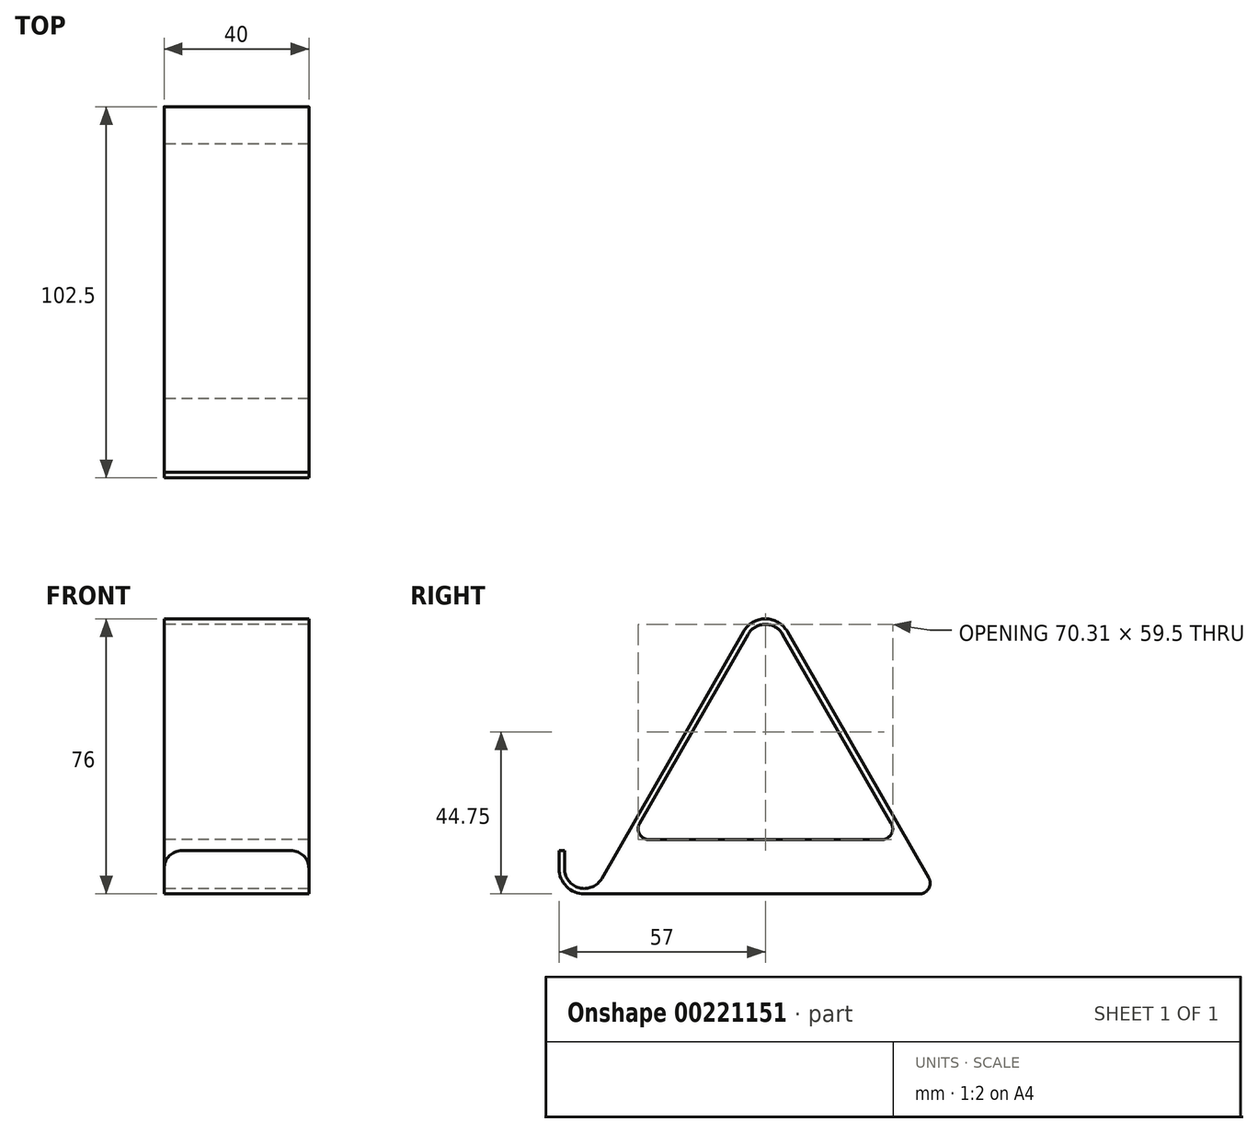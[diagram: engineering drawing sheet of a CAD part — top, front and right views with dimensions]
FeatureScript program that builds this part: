
annotation { "Feature Type Name" : "Feature", "Feature Type Description" : "" }
export const myFeature = defineFeature(function(context is Context, id is Id, definition is map)
    precondition{}
    {
        {
            var Q0;
            Q0=qCreatedBy(makeId("Right.planeOp"),FACE);
            var sketch = newSketch(context, id + "F0", { "sketchPlane" : qUnion([Q0])});
            skArc(sketch, "E0", {"start": v(-7, 0) * mm, "mid": v(-4.95, -4.95) * mm, "end": v(0, -7) * mm});
            skArc(sketch, "E1", {"start": v(54.77, 64.74) * mm, "mid": v(50, 67.5) * mm, "end": v(45.23, 64.74) * mm});
            skLineSegment(sketch, "E2", {"start": v(15.24, 12.5) * mm, "end": v(45.23, 64.74) * mm});
            skLineSegment(sketch, "E3", {"start": v(50, 62) * mm, "end": v(50, -12.6) * mm, "construction": true});
            skLineSegment(sketch, "E4.MirrorCS", {"start": v(84.76, 12.5) * mm, "end": v(54.77, 64.74) * mm});
            skLineSegment(sketch, "E5", {"start": v(0, -7) * mm, "end": v(92.5, -7) * mm, "construction": true});
            skLineSegment(sketch, "E6", {"start": v(-7, 0) * mm, "end": v(-7, 5) * mm});
            skLineSegment(sketch, "E7.0", {"start": v(-5.5, 0) * mm, "end": v(-5.5, 5) * mm});
            skLineSegment(sketch, "E7.1", {"start": v(95.1, -2.5) * mm, "end": v(56.07, 65.48) * mm});
            skArc(sketch, "E7.2", {"start": v(56.07, 65.48) * mm, "mid": v(50, 69) * mm, "end": v(43.93, 65.48) * mm});
            skLineSegment(sketch, "E7.3", {"start": v(4.77, -2.74) * mm, "end": v(43.93, 65.48) * mm});
            skArc(sketch, "E7.4", {"start": v(-5.5, 0) * mm, "mid": v(-1.42, -5.31) * mm, "end": v(4.77, -2.74) * mm});
            skLineSegment(sketch, "E8", {"start": v(0, -7) * mm, "end": v(97.68, -7) * mm});
            skLineSegment(sketch, "E9.trimOffspring", {"start": v(0, -7) * mm, "end": v(102.68, -7) * mm, "construction": true});
            skLineSegment(sketch, "E10.0", {"start": v(17.84, 8) * mm, "end": v(82.16, 8) * mm});
            skPoint(sketch, "E11.visualSharp", {"position": v(12.66, 8) * mm});
            skArc(sketch, "E11.filletArc", {"start": v(15.24, 12.5) * mm, "mid": v(15.25, 9.5) * mm, "end": v(17.84, 8) * mm});
            skPoint(sketch, "E12.visualSharp", {"position": v(87.34, 8) * mm});
            skArc(sketch, "E12.filletArc", {"start": v(82.16, 8) * mm, "mid": v(84.75, 9.5) * mm, "end": v(84.76, 12.5) * mm});
            skPoint(sketch, "E13.visualSharp", {"position": v(97.68, -7) * mm});
            skArc(sketch, "E13.filletArc", {"start": v(92.5, -7) * mm, "mid": v(95.1, -5.5) * mm, "end": v(95.1, -2.5) * mm});
            skLineSegment(sketch, "E14", {"start": v(-7, 5) * mm, "end": v(-5.5, 5) * mm});
            skSolve(sketch);
        }
        {
            var Q0;
            Q0 = qSketchRegion(id + "F0", true);
            extrude(context, id + "F1", {"entities" : qUnion([Q0]), "depth" : 40 * mm});
        }
        {
            var Q0;
            Q0=makeQuery(id+"F1.opExtrude","CAP_EDGE",EDGE,{"disambiguationData":[OSD([sQuery(id+"F0.wireOp",EDGE,"E14")])],"isStart":false});
            var Q1;
            Q1=makeQuery(id+"F1.opExtrude","CAP_EDGE",EDGE,{"disambiguationData":[OSD([sQuery(id+"F0.wireOp",EDGE,"E14")])],"isStart":true});
            fillet(context, id + "F2", {"entities" : qUnion([Q0, Q1]), "radius" : 5 * mm, "tangentPropagation" : true, "allowEdgeOverflow" : false});
        }
    });
